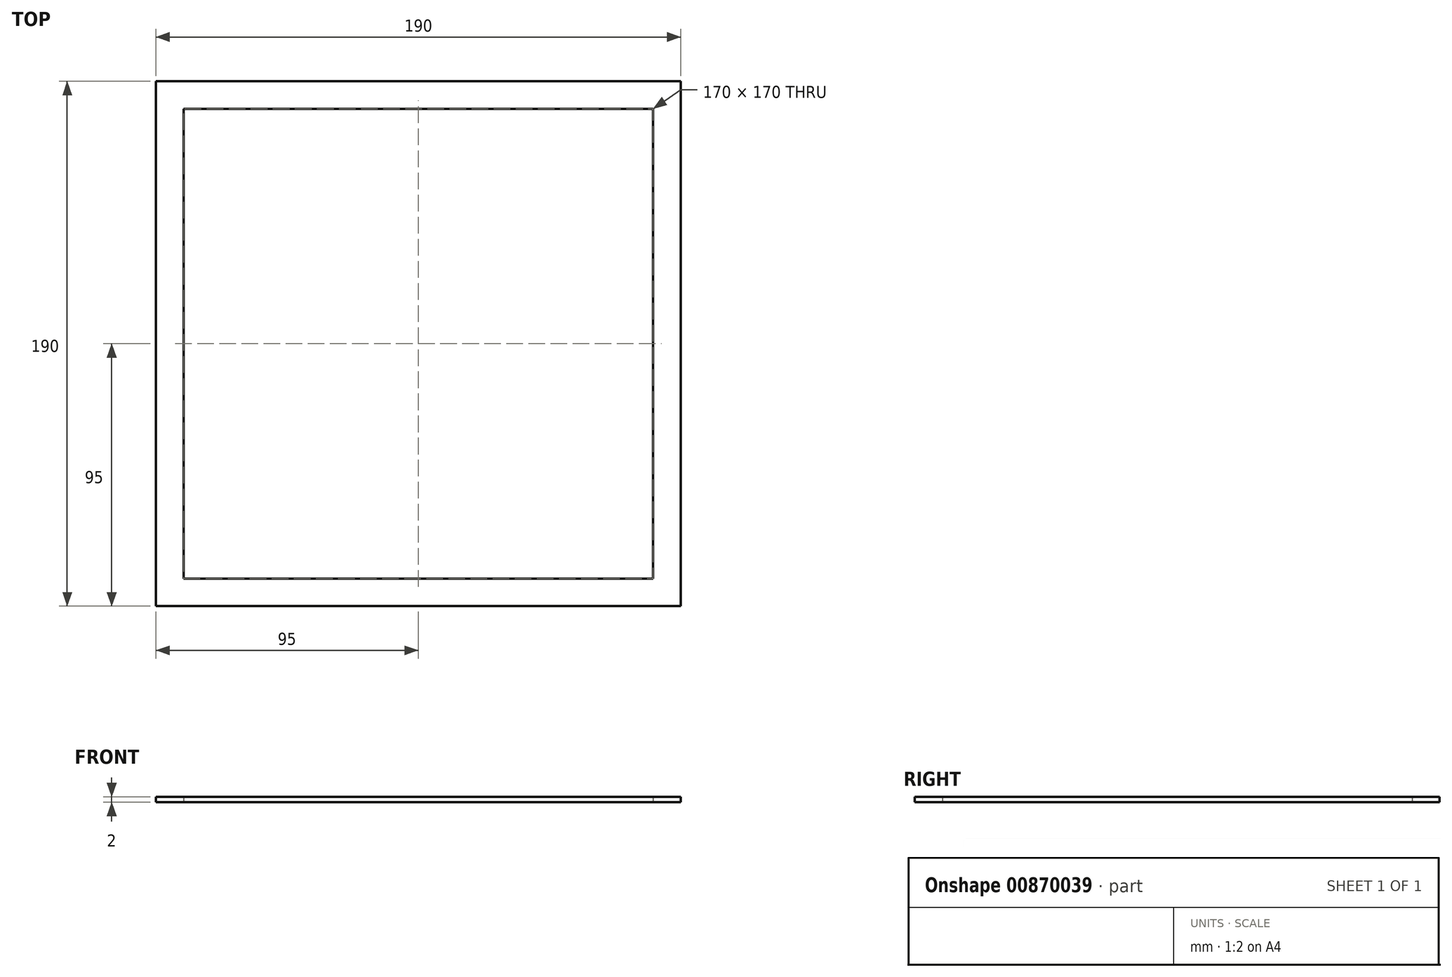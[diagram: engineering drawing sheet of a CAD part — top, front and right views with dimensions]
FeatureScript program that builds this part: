
annotation { "Feature Type Name" : "Feature", "Feature Type Description" : "" }
export const myFeature = defineFeature(function(context is Context, id is Id, definition is map)
    precondition{}
    {
        {
            var Q0;
            Q0=qCreatedBy(makeId("Top.planeOp"),FACE);
            var sketch = newSketch(context, id + "F0", { "sketchPlane" : qUnion([Q0])});
            skLineSegment(sketch, "E0.bottom", {"start": v(95, -95) * mm, "end": v(-95, -95) * mm});
            skLineSegment(sketch, "E0.top", {"start": v(95, 95) * mm, "end": v(-95, 95) * mm});
            skLineSegment(sketch, "E0.left", {"start": v(95, -95) * mm, "end": v(95, 95) * mm});
            skLineSegment(sketch, "E0.right", {"start": v(-95, -95) * mm, "end": v(-95, 95) * mm});
            skPoint(sketch, "E0.middle", {"position": v(0, 0) * mm});
            skLineSegment(sketch, "E1.0", {"start": v(-85, -85) * mm, "end": v(-85, 85) * mm});
            skLineSegment(sketch, "E1.1", {"start": v(85, -85) * mm, "end": v(-85, -85) * mm});
            skLineSegment(sketch, "E1.2", {"start": v(85, -85) * mm, "end": v(85, 85) * mm});
            skLineSegment(sketch, "E1.3", {"start": v(85, 85) * mm, "end": v(-85, 85) * mm});
            skSolve(sketch);
        }
        {
            var Q0;
            Q0=makeQuery(id+"F0.imprint","IMPRINT",FACE,{"disambiguationData":[TD([[makeQuery(id+"F0.imprint","IMPRINT",EDGE,{"derivedFrom":sQuery(id+"F0.wireOp",EDGE,"E0.bottom")}),-1.0]])]});
            extrude(context, id + "F1", {"entities" : qUnion([Q0]), "depth" : 2 * mm, "offsetDistance" : 25 * mm});
        }
    });
